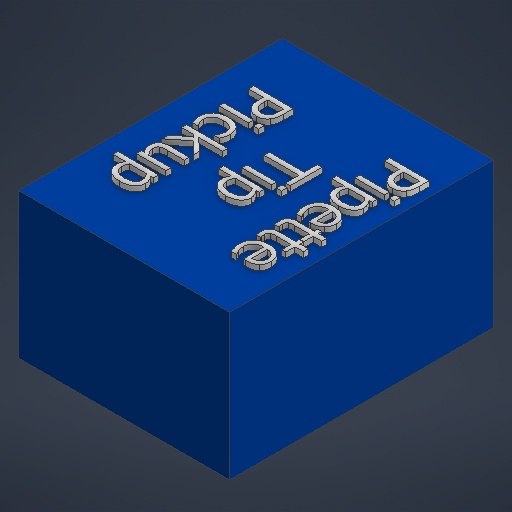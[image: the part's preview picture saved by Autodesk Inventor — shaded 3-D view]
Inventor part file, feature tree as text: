
AUTODESK INVENTOR PART (.ipt)
format: ipt  version: 2025.1 (Build 291241000, 241)  size: 556,032 bytes
history: native  units: mm
features: extrude x2, sketch x2
ambient origin geometry x8: Origin, YZ Plane, XZ Plane, XY Plane, X Axis, Y Axis, Z Axis, Center Point
bodies: Solid1 (feature_tree)
feature tree (4):
  extrude  "Extrusion1"  Depth=100.0mm
  extrude  "Extrusion2"  Depth=2.0mm TaperAngle=0.0deg
  sketch  "Sketch1"  dims[d0=80.0mm d1=100.0mm]
  sketch  "Sketch2"  dims[d2=55.0mm d3=0.0mm d4=2.0mm d5=0.0mm]
